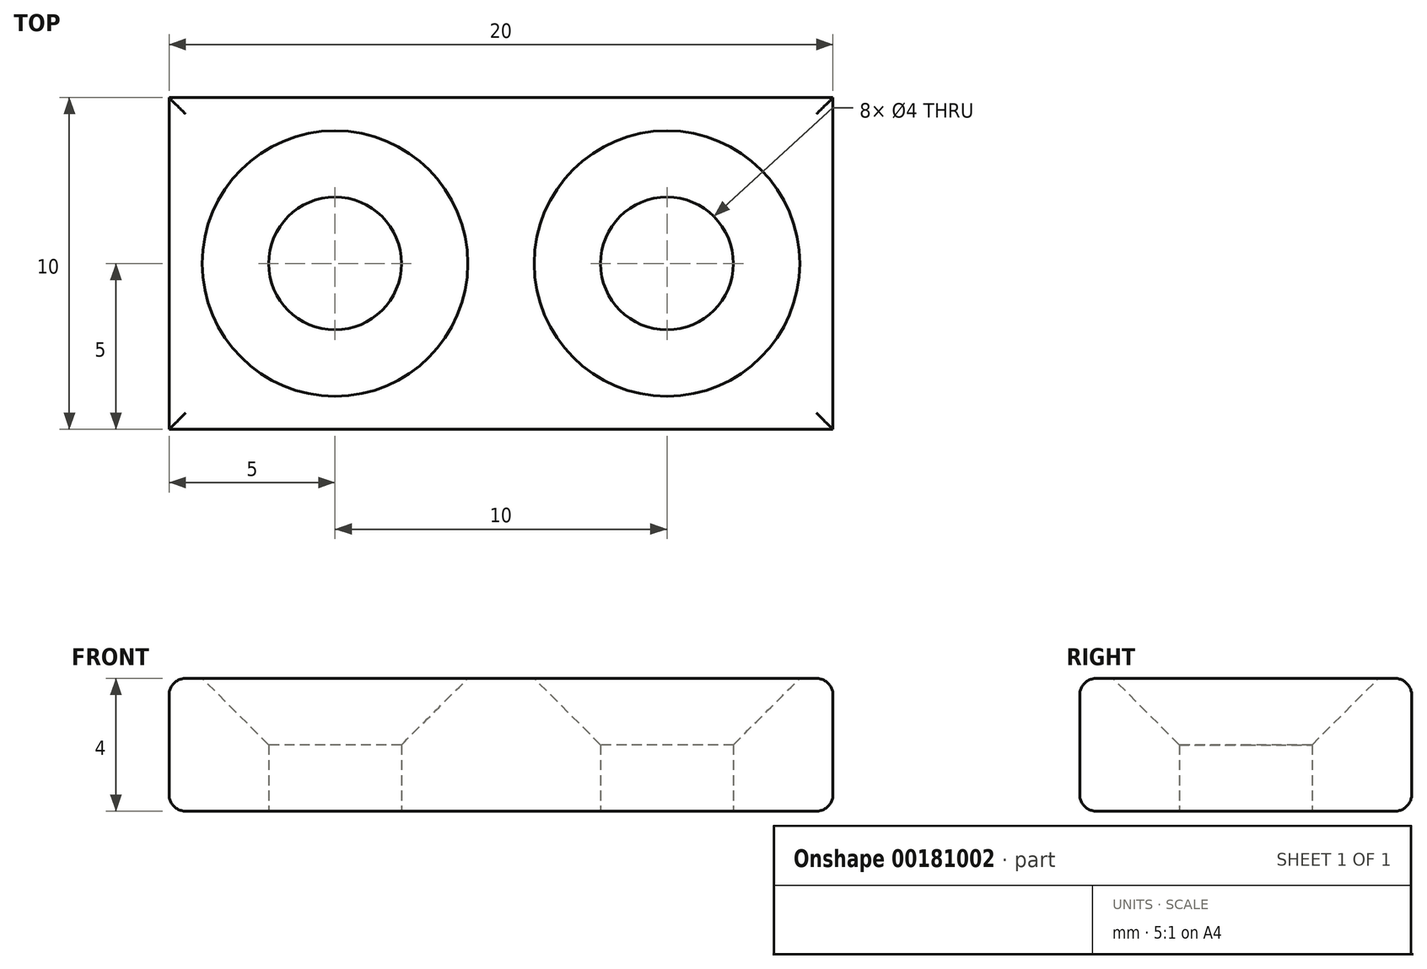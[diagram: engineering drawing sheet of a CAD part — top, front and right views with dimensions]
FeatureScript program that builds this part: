
annotation { "Feature Type Name" : "Feature", "Feature Type Description" : "" }
export const myFeature = defineFeature(function(context is Context, id is Id, definition is map)
    precondition{}
    {
        {
            var Q0;
            Q0=qCreatedBy(makeId("Top.planeOp"),FACE);
            var sketch = newSketch(context, id + "F0", { "sketchPlane" : qUnion([Q0])});
            skLineSegment(sketch, "E0.bottom", {"start": v(10, -5) * mm, "end": v(0, -5) * mm});
            skLineSegment(sketch, "E0.top", {"start": v(10, 5) * mm, "end": v(0, 5) * mm});
            skLineSegment(sketch, "E0.left", {"start": v(10, -5) * mm, "end": v(10, 5) * mm});
            skLineSegment(sketch, "E0.right", {"start": v(-10, -5) * mm, "end": v(-10, 5) * mm});
            skPoint(sketch, "E0.middle", {"position": v(0, 0) * mm});
            skLineSegment(sketch, "E1", {"start": v(0, 5) * mm, "end": v(0, -5) * mm, "construction": true});
            skLineSegment(sketch, "E2", {"start": v(0, -5) * mm, "end": v(-10, -5) * mm});
            skLineSegment(sketch, "E3", {"start": v(0, 5) * mm, "end": v(-10, 5) * mm});
            skCircle(sketch, "E4", {"center": v(-5, 0) * mm, "radius": 2 * mm});
            skPoint(sketch, "E4.centerSnap0", {"position": v(-5, 5) * mm});
            skCircle(sketch, "E5", {"center": v(5, 0) * mm, "radius": 2 * mm});
            skPoint(sketch, "E5.centerSnap0", {"position": v(10, 0) * mm});
            skPoint(sketch, "E5.centerSnap1", {"position": v(5, 5) * mm});
            skSolve(sketch);
        }
        {
            var Q0;
            Q0 = qSketchRegion(id + "F0", true);
            extrude(context, id + "F1", {"entities" : qUnion([Q0]), "depth" : 4 * mm});
        }
        {
            var Q0;
            Q0=makeQuery(id+"F1.opExtrude","CAP_EDGE",EDGE,{"disambiguationData":[OSD([sQuery(id+"F0.wireOp",EDGE,"E0.bottom"),sQuery(id+"F0.wireOp",EDGE,"E2")])],"isStart":false});
            var Q1;
            Q1=makeQuery(id+"F1.opExtrude","CAP_EDGE",EDGE,{"disambiguationData":[OSD([sQuery(id+"F0.wireOp",EDGE,"E0.right")])],"isStart":false});
            var Q2;
            Q2=makeQuery(id+"F1.opExtrude","CAP_EDGE",EDGE,{"disambiguationData":[OSD([sQuery(id+"F0.wireOp",EDGE,"E0.top"),sQuery(id+"F0.wireOp",EDGE,"E3")])],"isStart":false});
            var Q3;
            Q3=makeQuery(id+"F1.opExtrude","CAP_EDGE",EDGE,{"disambiguationData":[OSD([sQuery(id+"F0.wireOp",EDGE,"E0.left")])],"isStart":false});
            var Q4;
            Q4=makeQuery(id+"F1.opExtrude","CAP_EDGE",EDGE,{"disambiguationData":[OSD([sQuery(id+"F0.wireOp",EDGE,"E0.right")])],"isStart":true});
            var Q5;
            Q5=makeQuery(id+"F1.opExtrude","CAP_EDGE",EDGE,{"disambiguationData":[OSD([sQuery(id+"F0.wireOp",EDGE,"E0.bottom"),sQuery(id+"F0.wireOp",EDGE,"E2")])],"isStart":true});
            var Q6;
            Q6=makeQuery(id+"F1.opExtrude","CAP_EDGE",EDGE,{"disambiguationData":[OSD([sQuery(id+"F0.wireOp",EDGE,"E0.left")])],"isStart":true});
            var Q7;
            Q7=makeQuery(id+"F1.opExtrude","CAP_EDGE",EDGE,{"disambiguationData":[OSD([sQuery(id+"F0.wireOp",EDGE,"E0.top"),sQuery(id+"F0.wireOp",EDGE,"E3")])],"isStart":true});
            fillet(context, id + "F2", {"entities" : qUnion([Q0, Q1, Q2, Q3, Q4, Q5, Q6, Q7]), "radius" : 0.5 * mm, "tangentPropagation" : true, "allowEdgeOverflow" : false});
        }
        {
            var Q0;
            Q0=makeQuery(id+"F1.opExtrude","CAP_EDGE",EDGE,{"disambiguationData":[OSD([sQuery(id+"F0.wireOp",EDGE,"E5")])],"isStart":false});
            var Q1;
            Q1=makeQuery(id+"F1.opExtrude","CAP_EDGE",EDGE,{"disambiguationData":[OSD([sQuery(id+"F0.wireOp",EDGE,"E4")])],"isStart":false});
            chamfer(context, id + "F3", {"entities" : qUnion([Q0, Q1]), "width" : 2 * mm, "tangentPropagation" : true});
        }
    });
